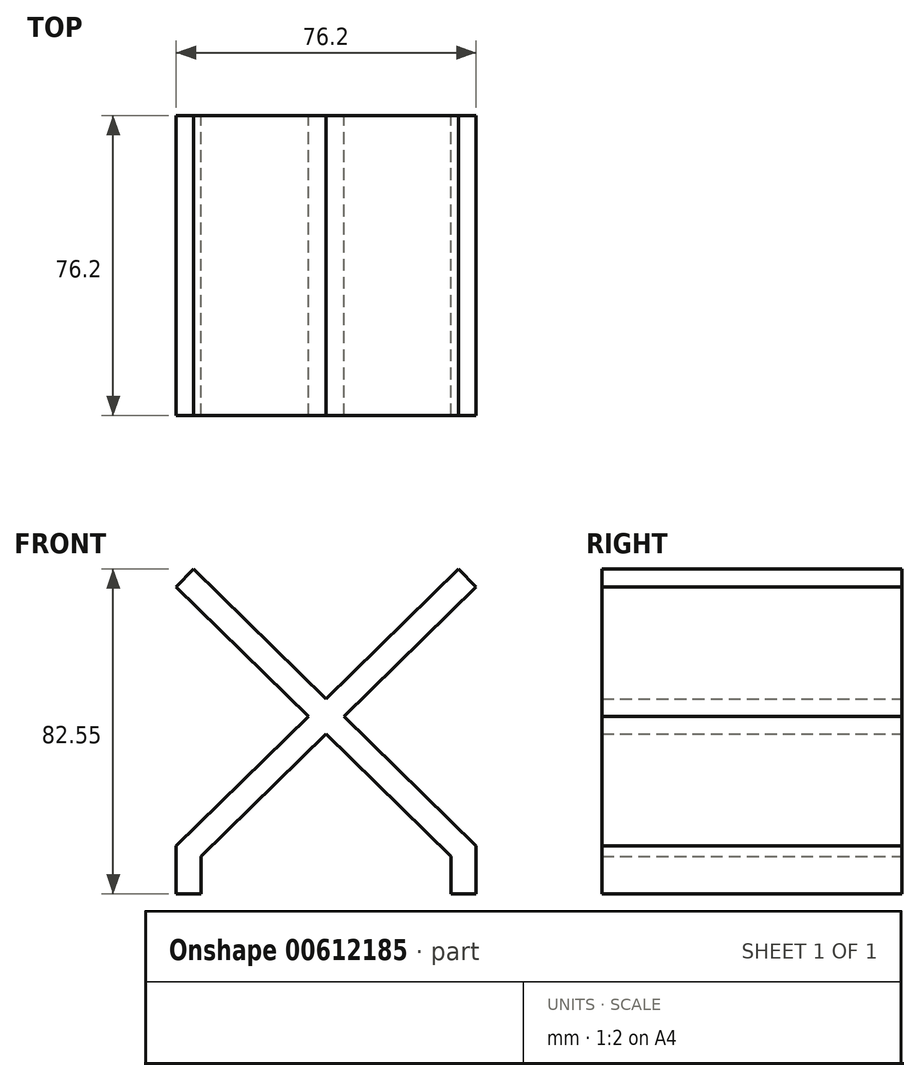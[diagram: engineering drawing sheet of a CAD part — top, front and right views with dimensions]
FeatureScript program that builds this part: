
annotation { "Feature Type Name" : "Feature", "Feature Type Description" : "" }
export const myFeature = defineFeature(function(context is Context, id is Id, definition is map)
    precondition{}
    {
        {
            var Q0;
            Q0=qCreatedBy(makeId("Front.planeOp"),FACE);
            var sketch = newSketch(context, id + "F0", { "sketchPlane" : qUnion([Q0])});
            skLineSegment(sketch, "E0", {"start": v(-38.1, -34.06) * mm, "end": v(-38.1, -21.88) * mm});
            skLineSegment(sketch, "E1", {"start": v(-31.75, -24.55) * mm, "end": v(-31.75, -34.06) * mm});
            skLineSegment(sketch, "E2", {"start": v(-31.75, -34.06) * mm, "end": v(-38.1, -34.06) * mm});
            skLineSegment(sketch, "E3", {"start": v(-31.75, -24.55) * mm, "end": v(0, 6.6) * mm});
            skLineSegment(sketch, "E4", {"start": v(38.1, 43.96) * mm, "end": v(33.65, 48.5) * mm});
            skLineSegment(sketch, "E5", {"start": v(33.65, 48.5) * mm, "end": v(0, 15.49) * mm});
            skLineSegment(sketch, "E6", {"start": v(38.1, -34.06) * mm, "end": v(31.75, -34.06) * mm});
            skLineSegment(sketch, "E7", {"start": v(31.75, -34.06) * mm, "end": v(31.75, -24.55) * mm});
            skLineSegment(sketch, "E8", {"start": v(31.75, -24.55) * mm, "end": v(0, 6.6) * mm});
            skLineSegment(sketch, "E9", {"start": v(-38.1, 43.96) * mm, "end": v(-33.65, 48.5) * mm});
            skLineSegment(sketch, "E10", {"start": v(-33.65, 48.5) * mm, "end": v(0, 15.49) * mm});
            skLineSegment(sketch, "E11", {"start": v(38.1, -21.88) * mm, "end": v(38.1, -34.06) * mm});
            skLineSegment(sketch, "E12.trimOffspring", {"start": v(4.53, 11.04) * mm, "end": v(38.1, 43.96) * mm});
            skLineSegment(sketch, "E13.trimOffspring", {"start": v(4.53, 11.04) * mm, "end": v(38.1, -21.88) * mm});
            skLineSegment(sketch, "E14.trimOffspring", {"start": v(-4.53, 11.04) * mm, "end": v(-38.1, -21.88) * mm});
            skLineSegment(sketch, "E15.trimOffspring", {"start": v(-4.53, 11.04) * mm, "end": v(-38.1, 43.96) * mm});
            skSolve(sketch);
        }
        {
            var Q0;
            Q0=makeQuery(id+"F0.imprint","IMPRINT",FACE,{"disambiguationData":[TD([[makeQuery(id+"F0.imprint","IMPRINT",EDGE,{"derivedFrom":sQuery(id+"F0.wireOp",EDGE,"E0")}),-1.0]])]});
            var Q1;
            Q1=sQuery(id+"F0.wireOp",EDGE,"E0");
            var Q2;
            Q2=sQuery(id+"F0.wireOp",EDGE,"E1");
            var Q3;
            Q3=sQuery(id+"F0.wireOp",EDGE,"E2");
            var Q4;
            Q4=sQuery(id+"F0.wireOp",EDGE,"E3");
            var Q5;
            Q5=sQuery(id+"F0.wireOp",EDGE,"E4");
            var Q6;
            Q6=sQuery(id+"F0.wireOp",EDGE,"E5");
            var Q7;
            Q7=sQuery(id+"F0.wireOp",EDGE,"E6");
            var Q8;
            Q8=sQuery(id+"F0.wireOp",EDGE,"E7");
            var Q9;
            Q9=sQuery(id+"F0.wireOp",EDGE,"E8");
            var Q10;
            Q10=sQuery(id+"F0.wireOp",EDGE,"E9");
            var Q11;
            Q11=sQuery(id+"F0.wireOp",EDGE,"E10");
            var Q12;
            Q12=sQuery(id+"F0.wireOp",EDGE,"E11");
            var Q13;
            Q13=sQuery(id+"F0.wireOp",EDGE,"E12.trimOffspring");
            var Q14;
            Q14=sQuery(id+"F0.wireOp",EDGE,"E13.trimOffspring");
            var Q15;
            Q15=sQuery(id+"F0.wireOp",EDGE,"E14.trimOffspring");
            var Q16;
            Q16=sQuery(id+"F0.wireOp",EDGE,"E15.trimOffspring");
            extrude(context, id + "F1", {"entities" : qUnion([Q0]), "surfaceEntities" : qUnion([Q1, Q2, Q3, Q4, Q5, Q6, Q7, Q8, Q9, Q10, Q11, Q12, Q13, Q14, Q15, Q16]), "depth" : 25.4 * mm, "offsetDistance" : 25.4 * mm, "hasSecondDirection" : true, "secondDirectionOppositeDirection" : true, "secondDirectionDepth" : 50.8 * mm});
        }
    });
